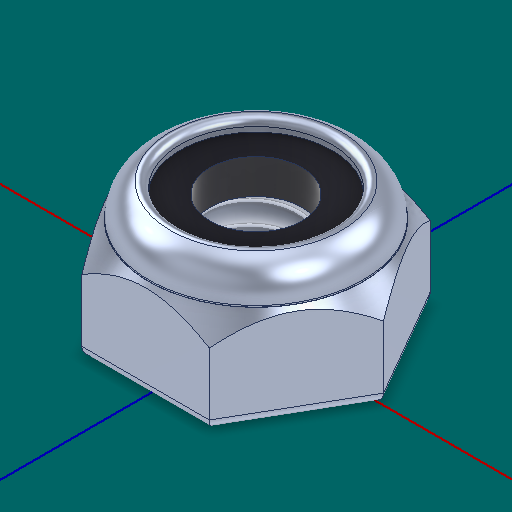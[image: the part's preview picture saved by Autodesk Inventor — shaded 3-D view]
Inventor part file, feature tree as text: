
AUTODESK INVENTOR PART (.ipt)
format: ipt  version: 2025 (Build 290162000, 162)  size: 232,448 bytes
history: native  units: in
note: dims shown in document units (in); Inventor stores cm internally (conversion verified against a paired STEP export)
features: other x4, sketch x2, plane x1
ambient origin geometry x8: Origin, YZ Plane, XZ Plane, XY Plane, X Axis, Y Axis, Z Axis, Center Point
bodies: Body1 (feature_tree)
feature tree (7):
  other  "Nut Thin Nylock_mirrored.ipt"
  other  "NONE::Nut Thin Nylock_mirrored.ipt"
  other  "TaggingFeature1"
  sketch  "Sketch1"  dims[d0=0.3937in]
  sketch  "Sketch2"
  plane  "Work Plane1"
  parser-record x1  (decoder bookkeeping rows leaked as tree rows — omitted from the tree; the rows remain in map.json)
